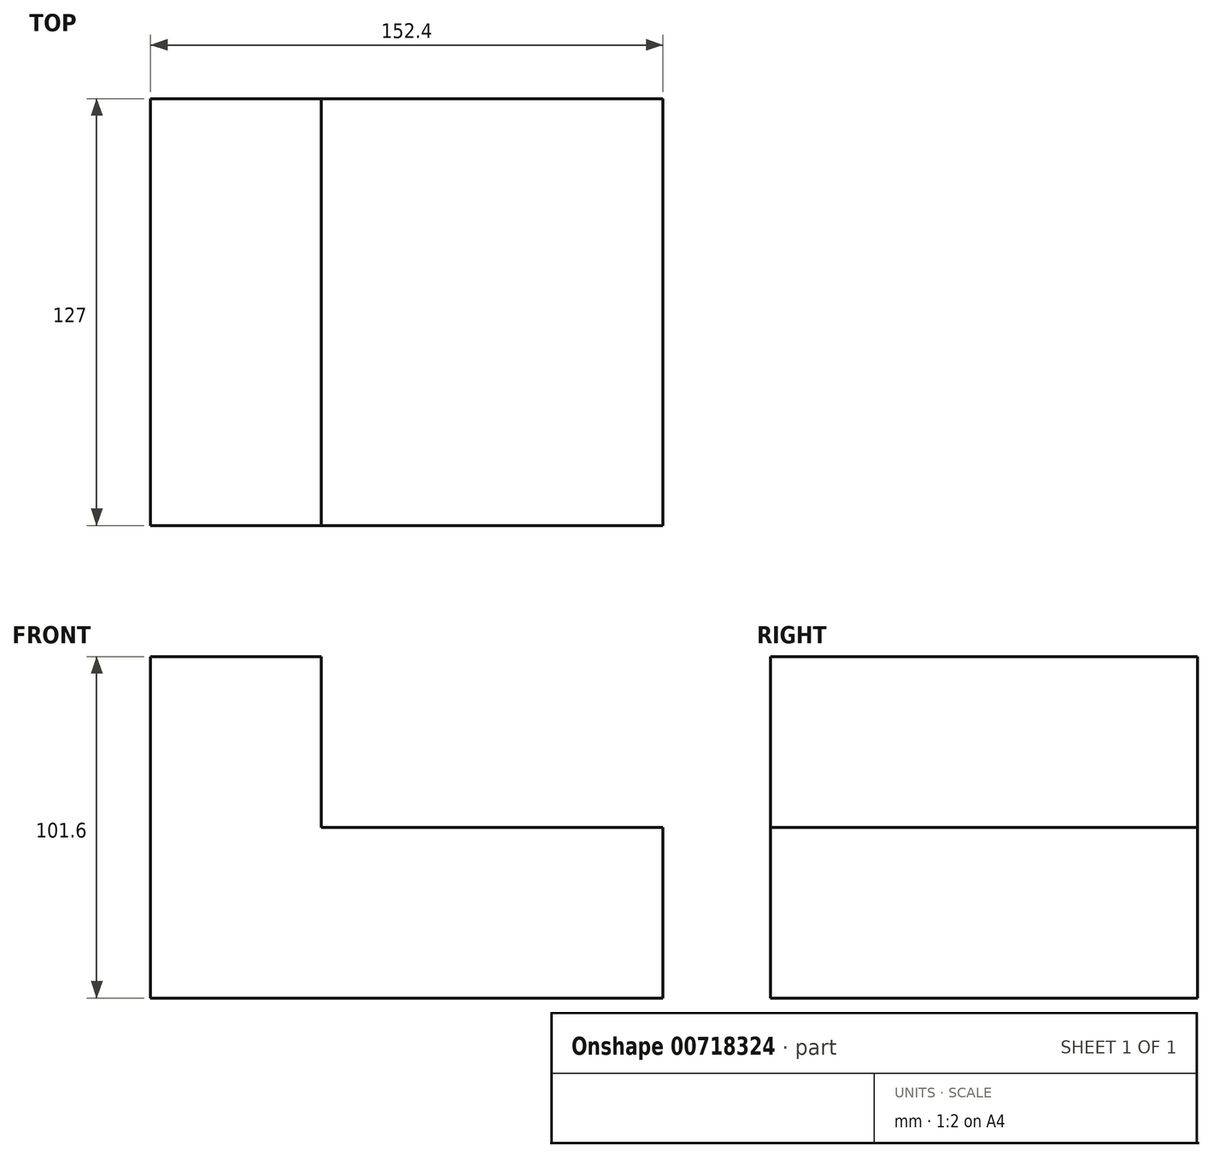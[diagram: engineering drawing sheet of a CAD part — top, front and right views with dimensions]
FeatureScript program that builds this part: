
annotation { "Feature Type Name" : "Feature", "Feature Type Description" : "" }
export const myFeature = defineFeature(function(context is Context, id is Id, definition is map)
    precondition{}
    {
        {
            var Q0;
            Q0=qCreatedBy(makeId("Front.planeOp"),FACE);
            var sketch = newSketch(context, id + "F0", { "sketchPlane" : qUnion([Q0])});
            skLineSegment(sketch, "E0", {"start": v(-91.77, -21.83) * mm, "end": v(60.63, -21.83) * mm});
            skLineSegment(sketch, "E1", {"start": v(60.63, -21.83) * mm, "end": v(60.63, 28.97) * mm});
            skLineSegment(sketch, "E2", {"start": v(60.63, 28.97) * mm, "end": v(-40.97, 28.97) * mm});
            skLineSegment(sketch, "E3", {"start": v(-40.97, 28.97) * mm, "end": v(-40.97, 79.77) * mm});
            skLineSegment(sketch, "E4", {"start": v(-40.97, 79.77) * mm, "end": v(-91.77, 79.77) * mm});
            skLineSegment(sketch, "E5", {"start": v(-91.77, 79.77) * mm, "end": v(-91.77, -21.83) * mm});
            skSolve(sketch);
        }
        {
            var Q0;
            Q0=makeQuery(id+"F0.imprint","IMPRINT",FACE,{"disambiguationData":[TD([[makeQuery(id+"F0.imprint","IMPRINT",EDGE,{"derivedFrom":sQuery(id+"F0.wireOp",EDGE,"E0")}),1.0]])]});
            extrude(context, id + "F1", {"entities" : qUnion([Q0]), "depth" : 127 * mm, "offsetDistance" : 25.4 * mm});
        }
    });
